# Revit family: LeL Intono B
name_source: partatom
category: Lighting Fixtures
units: mm (PartAtom-declared; Revit-internal decimal feet)

## family parameters
Always vertical = No
Cut with Voids When Loaded = No
Light Source = No
OmniClass Number = 23.80.70.00
OmniClass Title = Lighting
Part Type = Normal
Room Calculation Point = No
Round Connector Dimension = Use Diameter
Shared = No
Work Plane-Based = Yes

## types (6) — shared parameters
Apparent Load = 9 VA
CCT = 3000 K
CRI = CRI80
Default Elevation = 1219 mm
Description = Outdoor Bollard
IK = IK06
IP = IP66
Lamp = LED
Manufacturer = L&L Luce&Light srl
Rated Power supply = 230 V
URL = https://www.lucelight.it
Wattage = 9 W

## per-type parameters (varying)
| type | Height | Lumen Output | Model | Photometry |
| 1.0 A 9W | 300 mm | 307 lm | NB10 | NB1 Light source : A 9W |
| 1.1 A 9W | 600 mm | 307 lm | NB11 | NB1 Light source : A 9W |
| 1.2 A 9W | 800 mm  [stored 2.62467 ft] | 307 lm | NB12 | NB1 Light source : A 9W |
| 1.0 D 9W | 300 mm | 331 lm | NB10 | NB1 Light source : D 9W |
| 1.1 D 9W | 600 mm | 331 lm | NB11 | NB1 Light source : D 9W |
| 1.2 D 9W | 800 mm  [stored 2.62467 ft] | 331 lm | NB12 | NB1 Light source : D 9W |

note: [stored X ft] marks values corroborated as IEEE doubles in the binary element streams (Revit-internal decimal feet)

## geometry (parser evidence)
native form markers: Sweep x1
no freeform markers — native parametric forms only
